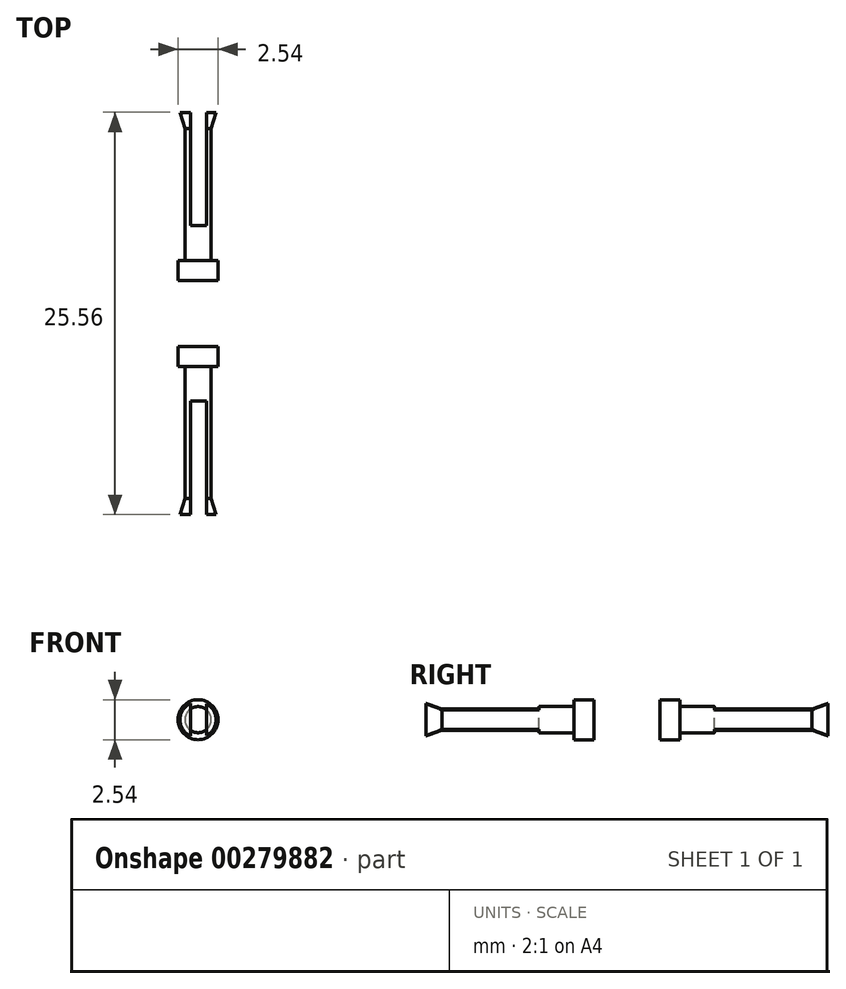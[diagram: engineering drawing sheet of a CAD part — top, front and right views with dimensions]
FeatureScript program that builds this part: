
annotation { "Feature Type Name" : "Feature", "Feature Type Description" : "" }
export const myFeature = defineFeature(function(context is Context, id is Id, definition is map)
    precondition{}
    {
        {
            var Q0;
            Q0=qCreatedBy(makeId("Top.planeOp"),FACE);
            var sketch = newSketch(context, id + "F0", { "sketchPlane" : qUnion([Q0])});
            skLineSegment(sketch, "E0", {"start": v(0, 2.1) * mm, "end": v(1.27, 2.1) * mm});
            skLineSegment(sketch, "E1", {"start": v(1.27, 2.1) * mm, "end": v(1.27, 3.38) * mm});
            skLineSegment(sketch, "E2", {"start": v(1.27, 3.38) * mm, "end": v(0.83, 3.38) * mm});
            skLineSegment(sketch, "E3", {"start": v(0.83, 3.38) * mm, "end": v(0.83, 12.78) * mm});
            skLineSegment(sketch, "E4", {"start": v(0.83, 12.78) * mm, "end": v(0, 12.78) * mm});
            skLineSegment(sketch, "E5", {"start": v(0, 12.78) * mm, "end": v(0, 2.1) * mm});
            skLineSegment(sketch, "E6", {"start": v(0.83, 12.78) * mm, "end": v(1.14, 12.78) * mm});
            skLineSegment(sketch, "E7", {"start": v(1.14, 12.78) * mm, "end": v(0.83, 11.76) * mm});
            skSolve(sketch);
        }
        {
            var Q0;
            Q0 = qSketchRegion(id + "F0", true);
            var Q1;
            Q1=sQuery(id+"F0.wireOp",EDGE,"E5");
            revolve(context, id + "F1", {"entities" : qUnion([Q0]), "axis" : qUnion([Q1]), "revolveType" : RevolveType.FULL});
        }
        {
            var Q0;
            Q0=qCreatedBy(makeId("Top.planeOp"),FACE);
            var sketch = newSketch(context, id + "F2", { "sketchPlane" : qUnion([Q0])});
            skLineSegment(sketch, "E8.bottom", {"start": v(0.54, 13.48) * mm, "end": v(-0.48, 13.48) * mm});
            skLineSegment(sketch, "E8.top", {"start": v(0.54, 5.57) * mm, "end": v(-0.48, 5.57) * mm});
            skLineSegment(sketch, "E8.left", {"start": v(0.54, 13.48) * mm, "end": v(0.54, 5.57) * mm});
            skLineSegment(sketch, "E8.right", {"start": v(-0.48, 13.48) * mm, "end": v(-0.48, 5.57) * mm});
            skSolve(sketch);
        }
        {
            var Q0;
            Q0 = qSketchRegion(id + "F2", true);
            extrude(context, id + "F3", {"entities" : qUnion([Q0]), "operationType" : NewBodyOperationType.REMOVE, "endBound" : BoundingType.THROUGH_ALL, "oppositeDirection" : true, "depth" : 25.4 * mm, "hasSecondDirection" : true, "secondDirectionOppositeDirection" : false, "secondDirectionDepth" : 25.4 * mm});
        }
        {
            var Q0;
            Q0=makeQuery(id+"F1.opRevolve","SWEPT_BODY",BODY,{"disambiguationData":[OSD([sQuery(id+"F0.wireOp",EDGE,"E0"),sQuery(id+"F0.wireOp",EDGE,"E1"),sQuery(id+"F0.wireOp",EDGE,"E2"),sQuery(id+"F0.wireOp",EDGE,"E3"),sQuery(id+"F0.wireOp",EDGE,"E4"),sQuery(id+"F0.wireOp",EDGE,"E5"),sQuery(id+"F0.wireOp",EDGE,"E6"),sQuery(id+"F0.wireOp",EDGE,"E7")])]});
            var Q1;
            Q1=qCreatedBy(makeId("Front.planeOp"),FACE);
            mirror(context, id + "F4", {"operationType" : NewBodyOperationType.ADD, "entities" : qUnion([Q0]), "mirrorPlane" : qUnion([Q1])});
        }
    });
